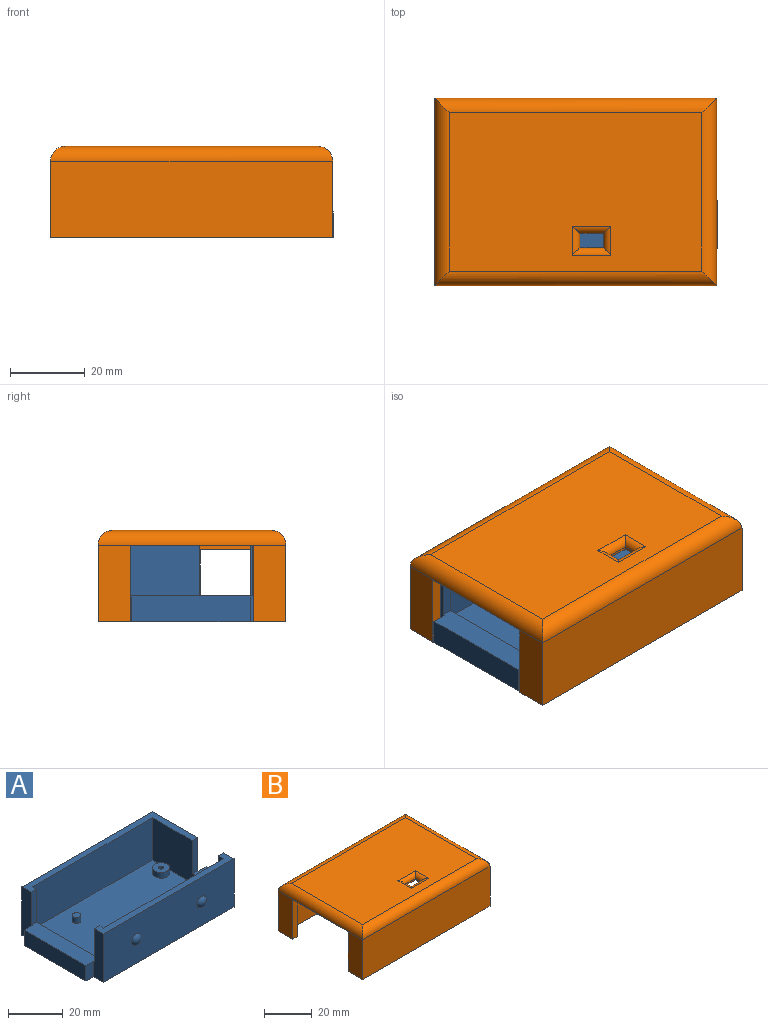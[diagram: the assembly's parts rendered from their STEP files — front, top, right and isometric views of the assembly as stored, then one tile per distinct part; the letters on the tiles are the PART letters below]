
ASSEMBLY  parts=2 mates=1
PART A: 46 faces, bbox 75.6x44.9x21.7 mm
  f0: plane 75.59x42.37mm, normal (0,0,-1), area 3043.7mm2, adj f2,f3,f5,f6,f11,f12,f13,f14
  f1: plane 13.77x6.66mm, normal (0,0,1), area 87.6mm2, adj f2,f3,f10,f11,f30,f31,f36,f37
  f2: plane 12.75x6.88mm, normal (1,0,0), area 87.8mm2, adj f0,f1,f36,f37
  f3: plane 23.9x21.72mm, normal (1,0,0), area 511.5mm2, adj f0,f1,f9,f12,f30,f37
  f4: plane 32.92x6.66mm, normal (0,0,1), area 215mm2, adj f5,f6,f8,f13,f32,f33,f34,f35
  f5: plane 31.9x6.88mm, normal (-1,0,0), area 219.6mm2, adj f0,f4,f34,f35
  f6: plane 21.72x5.23mm, normal (-1,0,0), area 106.1mm2, adj f0,f4,f9,f12,f33,f34
  f7: plane 67.67x5.21mm, normal (0,0,1), area 194.4mm2, adj f8,f10,f11,f13,f14,f16,f31,f32
  f8: plane 36.98x19.02mm, normal (1,0,0), area 215.3mm2, adj f4,f7,f9,f15,f16,f17,f32,f33
  f9: plane 67.67x23.39mm, normal (0,0,1), area 243.4mm2, adj f3,f6,f8,f10,f12,f15,f30,f33
  f10: plane 36.98x19.02mm, normal (-1,0,0), area 499.4mm2, adj f1,f7,f9,f15,f16,f17,f30,f31
  f11: plane 21.72x5.72mm, normal (1,0,0), area 116.6mm2, adj f0,f1,f7,f14,f31,f36
  f12: plane 67.67x21.72mm, normal (0,1,0), area 1434.1mm2, adj f0,f3,f6,f9,f44,f45
  f13: plane 21.72x5.23mm, normal (-1,0,0), area 106.1mm2, adj f0,f4,f7,f14,f32,f35
  f14: plane 67.67x21.72mm, normal (0,-1,0), area 1434.1mm2, adj f0,f7,f11,f13,f40,f41
  f15: plane 62.28x19.02mm, normal (0,-1,0), area 1184.9mm2, adj f8,f9,f10,f17
  f16: plane 62.28x19.02mm, normal (0,1,0), area 1184.9mm2, adj f7,f8,f10,f17
  f17: plane 62.28x36.98mm, normal (0,0,1), area 2224.1mm2, adj f8,f10,f15,f16,f19,f22,f24,f26
  f18: cylinder r=0.95mm len=3.81mm, axis (0,0,-1), area 22.8mm2, adj f20,f29
  f19: cylinder r=3.17mm len=6.35mm, axis (0,0,-1), area 50.7mm2, adj f17,f20
  f20: plane 6.35x6.35mm, normal (0,0,1), area 28.8mm2, adj f18,f19
  f21: cylinder r=0.95mm len=3.81mm, axis (0,0,-1), area 22.8mm2, adj f23,f28
  f22: cylinder r=3.17mm len=6.35mm, axis (0,0,-1), area 50.7mm2, adj f17,f23
  f23: plane 6.35x6.35mm, normal (0,0,1), area 28.8mm2, adj f21,f22
  f24: cylinder r=1.59mm len=3.18mm, axis (0,0,-1), area 25.3mm2, adj f17,f25
  f25: plane 3.18x3.18mm, normal (0,0,1), area 7.9mm2, adj f24
  f26: cylinder r=1.59mm len=3.18mm, axis (0,0,-1), area 25.3mm2, adj f17,f27
  f27: plane 3.18x3.18mm, normal (0,0,1), area 7.9mm2, adj f26
  f28: plane 1.91x1.91mm, normal (0,0,1), area 2.9mm2, adj f21
  f29: plane 1.91x1.91mm, normal (0,0,1), area 2.9mm2, adj f18
  f30: plane 14.83x2.69mm, normal (0,-1,0), area 39.9mm2, adj f1,f3,f9,f10
  f31: plane 14.83x2.69mm, normal (0,1,0), area 39.9mm2, adj f1,f7,f10,f11
  f32: plane 14.83x2.69mm, normal (0,1,0), area 39.9mm2, adj f4,f7,f8,f13
  f33: plane 14.83x2.69mm, normal (0,-1,0), area 39.9mm2, adj f4,f6,f8,f9
  f34: plane 6.88x3.96mm, normal (0,1,0), area 27.3mm2, adj f0,f4,f5,f6
  f35: plane 6.88x3.96mm, normal (0,-1,0), area 27.3mm2, adj f0,f4,f5,f13
  f36: plane 6.88x3.96mm, normal (0,-1,0), area 27.3mm2, adj f0,f1,f2,f11
  f37: plane 6.88x3.96mm, normal (0,1,0), area 27.3mm2, adj f0,f1,f2,f3
  f38: plane 0.04x0.04mm, normal (0,-1,0), area 0mm2, adj f41
  f39: plane 0.04x0.04mm, normal (0,-1,0), area 0mm2, adj f40
  f40: torus R=0.02mm, axis (0,1,0), area 22.8mm2, adj f14,f39
  f41: torus R=0.02mm, axis (0,1,0), area 22.8mm2, adj f14,f38
  f42: plane 0.04x0.04mm, normal (0,1,0), area 0mm2, adj f45
  f43: plane 0.04x0.04mm, normal (0,1,0), area 0mm2, adj f44
  f44: torus R=0.02mm, axis (0,-1,0), area 22.8mm2, adj f12,f43
  f45: torus R=0.02mm, axis (0,-1,0), area 22.8mm2, adj f12,f42
PART B: 30 faces, bbox 75.6x50.3x24.4 mm
  f0: plane 75.59x27.36mm, normal (0,0,-1), area 286.1mm2, adj f1,f4,f6,f7,f9,f11,f13,f21
  f1: plane 50.29x20.48mm, normal (1,0,0), area 766.1mm2, adj f0,f5,f7,f8,f19,f20,f21,f24
  f2: plane 70.21x44.91mm, normal (0,0,-1), area 3128.5mm2, adj f4,f9,f10,f11,f15,f16,f17,f18
  f3: plane 67.73x42.43mm, normal (0,0,1), area 2793.1mm2, adj f22,f23,f24,f25,f26,f27,f28,f29
  f4: plane 44.91x21.72mm, normal (1,0,0), area 301.8mm2, adj f0,f2,f5,f9,f10,f12,f13,f14
  f5: plane 75.59x9.17mm, normal (0,0,-1), area 237.1mm2, adj f1,f4,f6,f8,f10,f11,f14,f20
  f6: plane 50.29x20.48mm, normal (-1,0,0), area 356.5mm2, adj f0,f5,f7,f8,f12,f13,f14,f23
  f7: plane 75.59x20.48mm, normal (0,1,0), area 1548mm2, adj f0,f1,f6,f22
  f8: plane 75.59x20.48mm, normal (0,-1,0), area 1548mm2, adj f1,f5,f6,f25
  f9: plane 70.21x21.72mm, normal (0,-1,0), area 1524.7mm2, adj f0,f2,f4,f11
  f10: plane 70.21x21.72mm, normal (0,1,0), area 1524.7mm2, adj f2,f4,f5,f11
  f11: plane 44.91x21.72mm, normal (-1,0,0), area 711.4mm2, adj f0,f2,f5,f9,f10,f19,f20,f21
  f12: plane 32.92x2.69mm, normal (0,0,-1), area 88.6mm2, adj f4,f6,f13,f14
  f13: plane 20.46x2.69mm, normal (0,-1,0), area 55.1mm2, adj f0,f4,f6,f12
  f14: plane 20.46x2.69mm, normal (0,1,0), area 55.1mm2, adj f4,f5,f6,f12
  f15: plane 3.81x0.69mm, normal (-1,0,0), area 2.6mm2, adj f2,f16,f18,f26
  f16: plane 6.35x0.69mm, normal (0,-1,0), area 4.4mm2, adj f2,f15,f17,f27
  f17: plane 3.81x0.69mm, normal (1,0,0), area 2.6mm2, adj f2,f16,f18,f29
  f18: plane 6.35x0.69mm, normal (0,1,0), area 4.4mm2, adj f2,f15,f17,f28
  f19: plane 13.77x2.69mm, normal (0,0,-1), area 37.1mm2, adj f1,f11,f20,f21
  f20: plane 19.17x2.69mm, normal (0,1,0), area 51.6mm2, adj f1,f5,f11,f19
  f21: plane 19.17x2.69mm, normal (0,-1,0), area 51.6mm2, adj f0,f1,f11,f19
  f22: cylinder r=3.93mm len=75.59mm, axis (-1,0,0), area 449mm2, adj f3,f7,f23,f24
  f23: cylinder r=3.93mm len=50.29mm, axis (0,-1,0), area 292.8mm2, adj f3,f6,f22,f25
  f24: cylinder r=3.93mm len=50.29mm, axis (0,1,0), area 292.8mm2, adj f1,f3,f22,f25
  f25: cylinder r=3.93mm len=75.59mm, axis (1,0,0), area 449mm2, adj f3,f8,f23,f24
  f26: cylinder r=2mm len=7.81mm, axis (0,-1,0), area 16.5mm2, adj f3,f15,f27,f28
  f27: cylinder r=2mm len=10.35mm, axis (1,0,0), area 24.5mm2, adj f3,f16,f26,f29
  f28: cylinder r=2mm len=10.35mm, axis (-1,0,0), area 24.5mm2, adj f3,f18,f26,f29
  f29: cylinder r=2mm len=7.81mm, axis (0,1,0), area 16.5mm2, adj f3,f17,f27,f28
PLACE A t=(-12.72,-7.57,0)mm
PLACE B t=(-12.95,-7.9,0.07)mm
MATE slider B.f3 <-> A.f17  axis (0,0,1) through (-13.07,-7.52,21.79)mm
